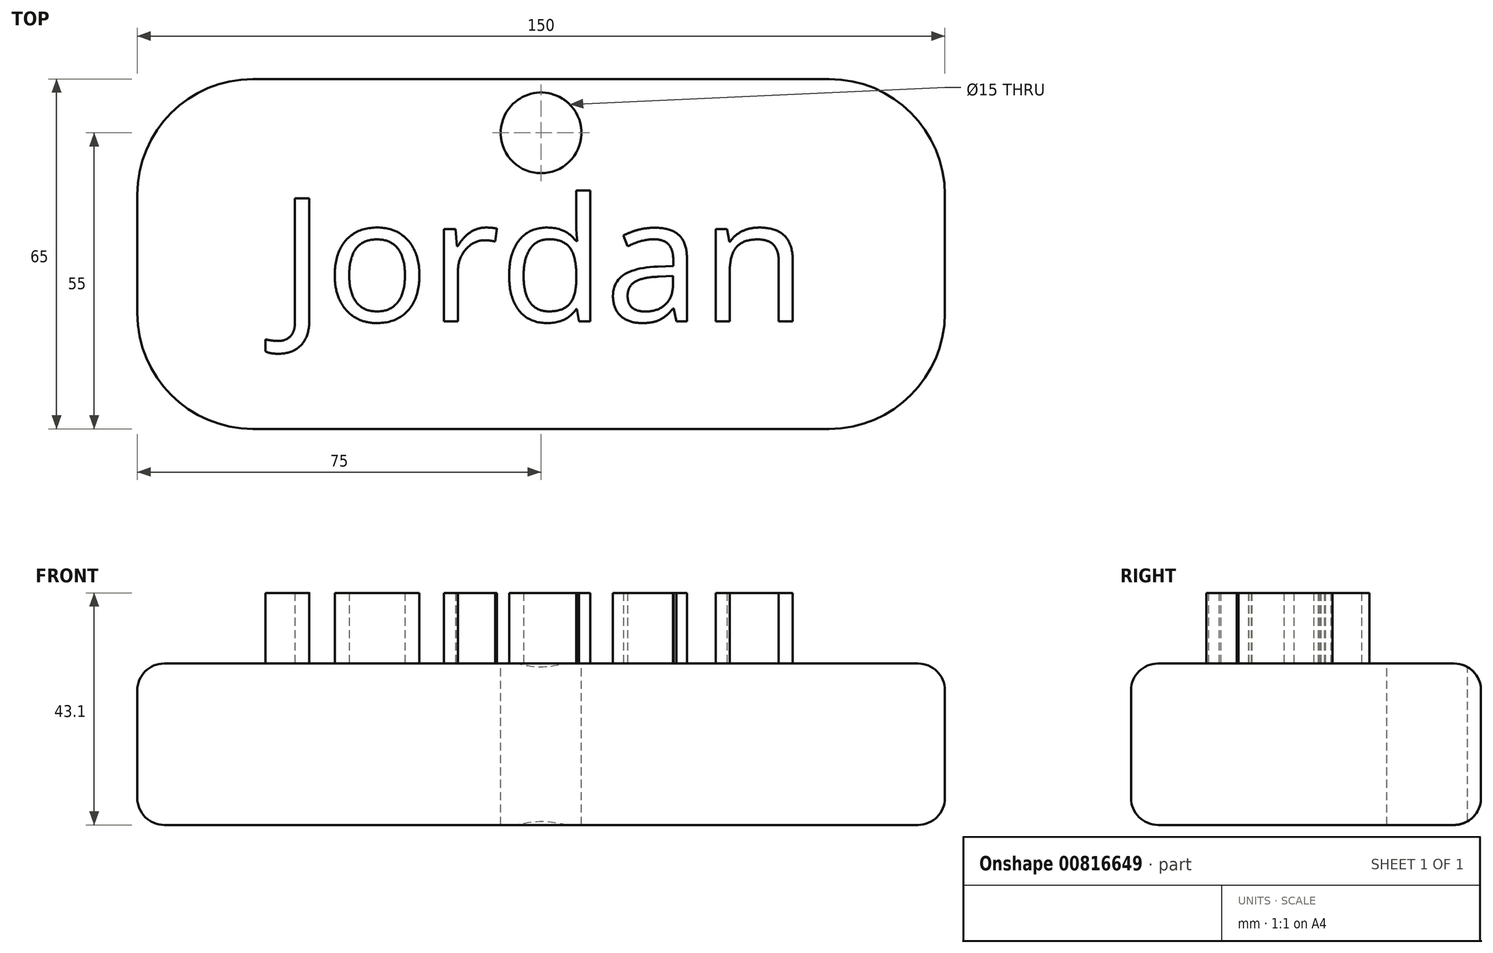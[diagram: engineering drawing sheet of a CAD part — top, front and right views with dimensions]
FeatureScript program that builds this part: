
annotation { "Feature Type Name" : "Feature", "Feature Type Description" : "" }
export const myFeature = defineFeature(function(context is Context, id is Id, definition is map)
    precondition{}
    {
        {
            var Q0;
            Q0=qCreatedBy(makeId("Top.planeOp"),FACE);
            var sketch = newSketch(context, id + "F0", { "sketchPlane" : qUnion([Q0])});
            skLineSegment(sketch, "E0.bottom", {"start": v(75, 32.5) * mm, "end": v(-75, 32.5) * mm});
            skLineSegment(sketch, "E0.top", {"start": v(75, -32.5) * mm, "end": v(-75, -32.5) * mm});
            skLineSegment(sketch, "E0.left", {"start": v(75, 32.5) * mm, "end": v(75, -32.5) * mm});
            skLineSegment(sketch, "E0.right", {"start": v(-75, 32.5) * mm, "end": v(-75, -32.5) * mm});
            skPoint(sketch, "E0.middle", {"position": v(0, 0) * mm});
            skSolve(sketch);
        }
        {
            var Q0;
            Q0=makeQuery(id+"F0.imprint","IMPRINT",FACE,{"disambiguationData":[TD([[makeQuery(id+"F0.imprint","IMPRINT",EDGE,{"derivedFrom":sQuery(id+"F0.wireOp",EDGE,"E0.bottom")}),1.0]])]});
            extrude(context, id + "F1", {"entities" : qUnion([Q0]), "depth" : 30 * mm, "offsetDistance" : 25 * mm});
        }
        {
            var Q0;
            Q0=makeQuery(id+"F1.opExtrude","CAP_FACE",FACE,{"disambiguationData":[OSD([sQuery(id+"F0.wireOp",EDGE,"E0.bottom"),sQuery(id+"F0.wireOp",EDGE,"E0.top"),sQuery(id+"F0.wireOp",EDGE,"E0.left"),sQuery(id+"F0.wireOp",EDGE,"E0.right")])],"isStart":false});
            var sketch = newSketch(context, id + "F2", { "sketchPlane" : qUnion([Q0])});
            skText(sketch, "E1", { "text": "Jordan", "fontName": "OpenSans-Regular.ttf"});
            const initialGuessF2  = {"E1": [-0.04867, -0.01253, 1, 0, 0.02304]};
            skSetInitialGuess(sketch, initialGuessF2);
            skSolve(sketch);
        }
        {
            var Q0;
            Q0 = qSketchRegion(id + "F2", true);
            extrude(context, id + "F3", {"entities" : qUnion([Q0]), "operationType" : NewBodyOperationType.ADD, "depth" : 13.1 * mm, "offsetDistance" : 25 * mm});
        }
        {
            var Q0;
            {var subQ0=sQuery(id+"F0.wireOp",EDGE,"E0.left");var subQ1=sQuery(id+"F0.wireOp",EDGE,"E0.bottom");var subQ2=sQuery(id+"F0.wireOp",EDGE,"E0.right");var subQ3=sQuery(id+"F0.wireOp",EDGE,"E0.top");Q0=makeQuery(id+"F3.boolean.opBoolean","SPLIT",FACE,{"disambiguationData":[TD([makeQuery(id+"F1.opExtrude","SWEPT_FACE",FACE,{"disambiguationData":[OSD([subQ1])]})])],"derivedFrom":makeQuery(id+"F1.opExtrude","CAP_FACE",FACE,{"disambiguationData":[OSD([subQ1,subQ3,subQ0,subQ2])],"isStart":false})});}
            var sketch = newSketch(context, id + "F4", { "sketchPlane" : qUnion([Q0])});
            skCircle(sketch, "E2", {"center": v(0, 22.5) * mm, "radius": 7.5 * mm});
            skLineSegment(sketch, "E3", {"start": v(0, 32.5) * mm, "end": v(0, 22.5) * mm});
            skSolve(sketch);
        }
        {
            var Q0;
            Q0 = qSketchRegion(id + "F4", true);
            extrude(context, id + "F5", {"entities" : qUnion([Q0]), "operationType" : NewBodyOperationType.REMOVE, "oppositeDirection" : true, "depth" : 82.4 * mm, "offsetDistance" : 25 * mm});
        }
        {
            var Q0;
            Q0=makeQuery(id+"F1.opExtrude","SWEPT_EDGE",EDGE,{"disambiguationData":[OSD([sQuery(id+"F0.wireOp",EDGE,"E0.bottom"),sQuery(id+"F0.wireOp",EDGE,"E0.right")])]});
            var Q1;
            Q1=makeQuery(id+"F1.opExtrude","SWEPT_EDGE",EDGE,{"disambiguationData":[OSD([sQuery(id+"F0.wireOp",EDGE,"E0.top"),sQuery(id+"F0.wireOp",EDGE,"E0.right")])]});
            var Q2;
            Q2=makeQuery(id+"F1.opExtrude","SWEPT_EDGE",EDGE,{"disambiguationData":[OSD([sQuery(id+"F0.wireOp",EDGE,"E0.top"),sQuery(id+"F0.wireOp",EDGE,"E0.left")])]});
            var Q3;
            Q3=makeQuery(id+"F1.opExtrude","SWEPT_EDGE",EDGE,{"disambiguationData":[OSD([sQuery(id+"F0.wireOp",EDGE,"E0.bottom"),sQuery(id+"F0.wireOp",EDGE,"E0.left")])]});
            fillet(context, id + "F6", {"entities" : qUnion([Q0, Q1, Q2, Q3]), "radius" : 21.49 * mm, "tangentPropagation" : true, "allowEdgeOverflow" : false});
        }
        {
            var Q0;
            Q0=makeQuery(id+"F1.opExtrude","CAP_EDGE",EDGE,{"disambiguationData":[OSD([sQuery(id+"F0.wireOp",EDGE,"E0.top")])],"isStart":false});
            var Q1;
            Q1=makeQuery(id+"F1.opExtrude","CAP_EDGE",EDGE,{"disambiguationData":[OSD([sQuery(id+"F0.wireOp",EDGE,"E0.top")])],"isStart":true});
            fillet(context, id + "F7", {"entities" : qUnion([Q0, Q1]), "radius" : 5 * mm, "tangentPropagation" : true, "allowEdgeOverflow" : false});
        }
    });
